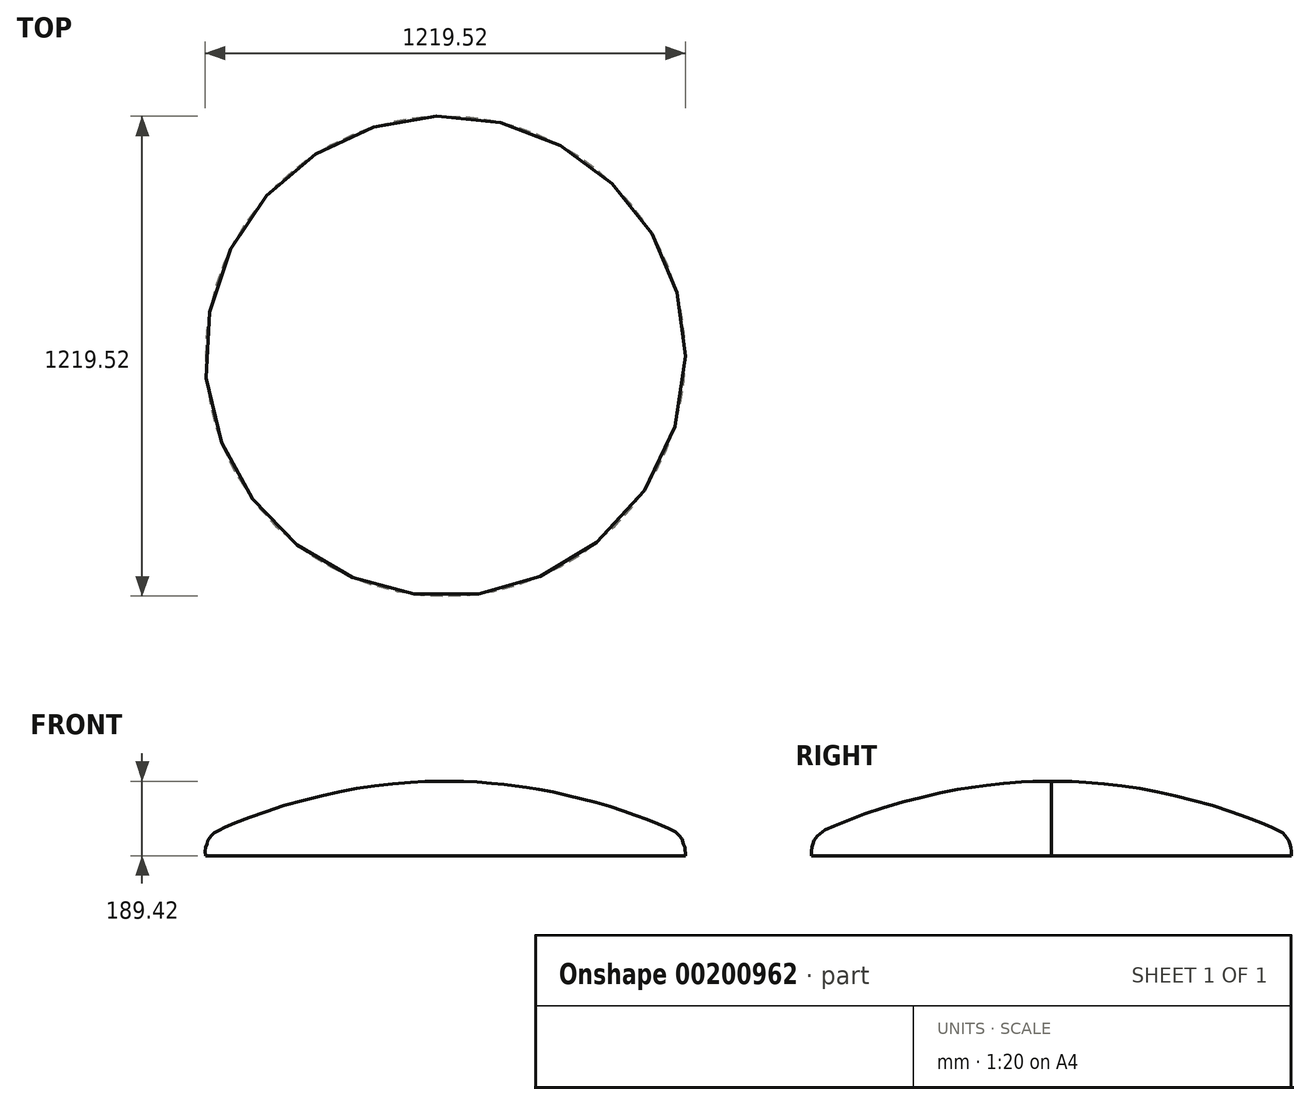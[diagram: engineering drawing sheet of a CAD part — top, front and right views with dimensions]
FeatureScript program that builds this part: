
annotation { "Feature Type Name" : "Feature", "Feature Type Description" : "" }
export const myFeature = defineFeature(function(context is Context, id is Id, definition is map)
    precondition{}
    {
        {
            var Q0;
            Q0=qCreatedBy(makeId("Front.planeOp"),FACE);
            var sketch = newSketch(context, id + "F0", { "sketchPlane" : qUnion([Q0])});
            skLineSegment(sketch, "E0", {"start": v(0, 0) * mm, "end": v(0, 411.95) * mm});
            skFitSpline(sketch, "E1", {"points": [v(0, 189.38) * mm, v(61.75, 188.41) * mm, v(137.4, 182.1) * mm, v(185.92, 176.3) * mm, v(247.63, 166.7) * mm, v(327.53, 148.87) * mm, v(409.4, 127.53) * mm, v(480.05, 103.6) * mm, v(533.39, 83.42) * mm, v(575.2, 64.68) * mm, v(588.31, 57.05) * mm, v(593.97, 51.05) * mm, v(599.28, 44.54) * mm, v(605.11, 33.56) * mm, v(605.97, 24.82) * mm, v(608.2, 22.42) * mm, v(609.6, 0) * mm], "startDerivative": vector(715.55, 2.54) * mm, "endDerivative": vector(-14.24, -583.16) * mm});
            skLineSegment(sketch, "E2", {"start": v(0, 0) * mm, "end": v(609.6, 0) * mm});
            skSolve(sketch);
        }
        {
            var Q0;
            Q0 = qSketchRegion(id + "F0", true);
            var Q1;
            Q1=sQuery(id+"F0.wireOp",EDGE,"E0");
            revolve(context, id + "F1", {"surfaceOperationType" : NewSurfaceOperationType.NEW, "entities" : qUnion([Q0]), "axis" : qUnion([Q1]), "revolveType" : RevolveType.FULL});
        }
    });
